# Revit family: Rough-In_Valve-3-Way_Diveter-Grohe-29903000
name_source: partatom
category: Plumbing Fixtures
units: mm (PartAtom-declared; Revit-internal decimal feet)

## family parameters
Cut with Voids When Loaded = No
Host = Face
OmniClass Number = 23.65.55.14.11
OmniClass Title = Inlet/Outlet Valves for Liquid Services
Part Type = Normal
Room Calculation Point = No
Round Connector Dimension = Use Radius
Shared = Yes

## types (1)
- 29903000
    ADA Compliant = Yes
    Assembly Code = D2010710
    CW Connection = Yes
    CWFU = 0
    CalGreen Compliant = Yes
    Cold Water Connection Diameter = 1/2"
    Cold Water Connection Radius = 1/4"
    Default Elevation = 40"
    Description = 3-Way Diverter Rough-In Valve (Shared Functions)
    Finish = Brass-Grohe-Chrome
    HW Connection = Yes
    HWFU = 0
    Height = 3 1/8"
    Hot Water Connection Diameter = 1"
    Hot Water Connection Radius = 1/4"
    Installation Type = Wall Mounted
    Length = 3 1/8"
    Manufacturer = Grohe
    Material = Brass-Grohe-Chrome
    Model = 29903000
    Price = Prices may vary. Please consult Manufacturer Representative for most up-to-date price list.
    Product Documentation Link = https://americanstandard.box.com
    Product Page URL = https://www.grohe.us
    Tempered Water Connection Diameter = 1/2"
    Tempered Water Connection Radius = 1/4"
    Tub Connection Diameter = 1/2"
    Tub Connection Radius = 1/4"
    Tub Port = Yes
    Tub Port Connection Description = 1/2'' NPT Tub Port Outlet
    URL = https://www.grohe.us
    Vent Connection = No
    WFU = 0
    Warranty Documentation Link = https://www.grohe.us
    Warranty Information = Limited lifetime warranty
    Waste Connection = No
    Width = 3 1/8"

## geometry (parser evidence)
native form markers: Sweep x2
no freeform markers — native parametric forms only
